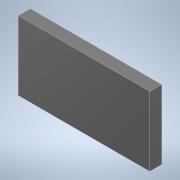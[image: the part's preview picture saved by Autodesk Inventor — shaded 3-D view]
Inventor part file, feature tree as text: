
AUTODESK INVENTOR PART (.ipt)
format: ipt  version: 2021 (Build 250183000, 183)  size: 91,136 bytes
history: native  units: mm
features: other x1, extrude x1, sketch x1
ambient origin geometry x8: Origin, YZ Plane, XZ Plane, XY Plane, X Axis, Y Axis, Z Axis, Center Point
bodies: Body1 (feature_tree)
feature tree (3):
  other  "Sólido1"
  extrude  "Extrusão1"  Depth=29.0mm
  sketch  "Esboço1"  dims[d0=55.0mm d1=29.0mm d2=5.0mm d3=0.0mm]
